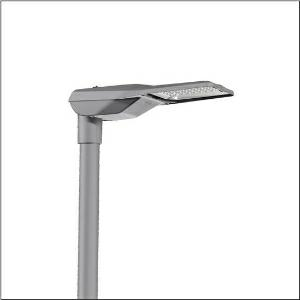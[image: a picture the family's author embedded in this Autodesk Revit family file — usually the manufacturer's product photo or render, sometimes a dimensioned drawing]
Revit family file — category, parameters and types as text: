
# Revit family: streetlight_sl_21_mini___stw1_0a_5xe2e33s08hb_4f98
name_source: partatom
category: Lighting Fixtures
units: mm (PartAtom-declared; Revit-internal decimal feet)

## family parameters
Cut with Voids When Loaded = No
Host = Face
Light Source = No
Part Type = Normal
Room Calculation Point = No
Round Connector Dimension = Use Diameter
Shared = No

## types (1)
- --- (1 x LED, 9040 lm, 66 W, 3000K)
    Apparent Load = 66 VA
    CIE Flux Codes = 38 75 98 100 100
    Color Rendering = 70
    Color Temperature = 3000K
    Default Elevation = 1800 mm
    Description = Streetlight SL 21 mini, mast luminaire, primary light control with lens, of PMMA, primary optical cover: cover, of toughened safety glass, transparent, light distribution: STW1.0a, light emission: direct distribution, primary light characteristic: asymmetric, installation type: side-entry, post-top, LED, High Power LED, rated luminous flux: 9.040lm, luminous efficacy: 137lm/W, light colour: 730, colour temperature: 3000K, control gear: D4i, control: overheat protection, constant luminous flux control, time-dependent luminous flux control, flexible luminous flux parameterisation, pre-setting: logarithmic dimming characteristic, mains connection: 220..240V, AC, 50/60Hz, start of lifetime: 66W, end of service life: 69W, reduction: 30W, luminaire housing, of diecast aluminium, powder-coated, Siteco® metallic grey (DB 702S), corrosivity category C5 mid according to DIN EN ISO 12944, please order mast flange separately, inclination adjustable: 0°, 5°, 10°, 15°, sealing non-destructively replaceable, multi-level sealing system, length: 628mm, width: 235mm, height: 110mm, mast flange for spigot size: 42mm (side-entry): 5XC10008XM4, 60/48mm (side-entry/post-top): 5XC10108XM2, 76/60mm (side-entry/post-top): 5XC10108XM1, mounting height: 4..8m, Smart Interface above, protection rating (complete): IP66, insulation class (complete): insulation class II (safety insulation), certification: CE, ENEC, ENEC+, VDE, impact resistance: IK10, permissible operating ambient temperature for outdoor applications: -40..+50°C, standard-compliant lighting for roads and squares, packaging unit: 1 piece

Light Distribution: STW1.0a
    Height = 110 mm
    Lamp = 1 x LED
    Lamp Light Flux = 9040 lm
    Lamp Power = 66 W
    Lamp count = 1
    Length = 625 mm
    Luminous efficacy = 137 lm/W
    Manufacturer = Siteco
    ModVariant = No
    Model = 5XE2E33S08HB
    Number of Poles = 1
    OnlyDefault = Yes
    Power Factor = 1
    Product Name = Streetlight SL 21 mini | STW1.0a
    Product group = mast luminaire | pylon top
    ProductGroupID = 6100
    Protection Class = Protection class II
    Protection Degree = IP 66
    RLX_Detail_Level = 1
    RLX_Emergency_Light_Flux = 0 lm
    RLX_Emergency_Type = 0
    RLX_Emergency_Type_DB = No
    RlxData = <blob elided: 26133 chars, md5=af168645>
    Socket = socket
    Standby Power = 0 W
    System Light Flux = 9040 lm
    System Power = 66 W
    Type Comments = factory setting: luminous flux: 100 % | dim-lin: 254 | 670 mA
    Type Image = l_1003515.jpg
    URL = http://relux.com
    VarID = @adj_187370
    Voltage = 0 V
    Weight = 0.00 kg
    Width = 234 mm

## geometry (parser evidence)
native form markers: Blend x4, Sweep x13
no freeform markers — native parametric forms only
